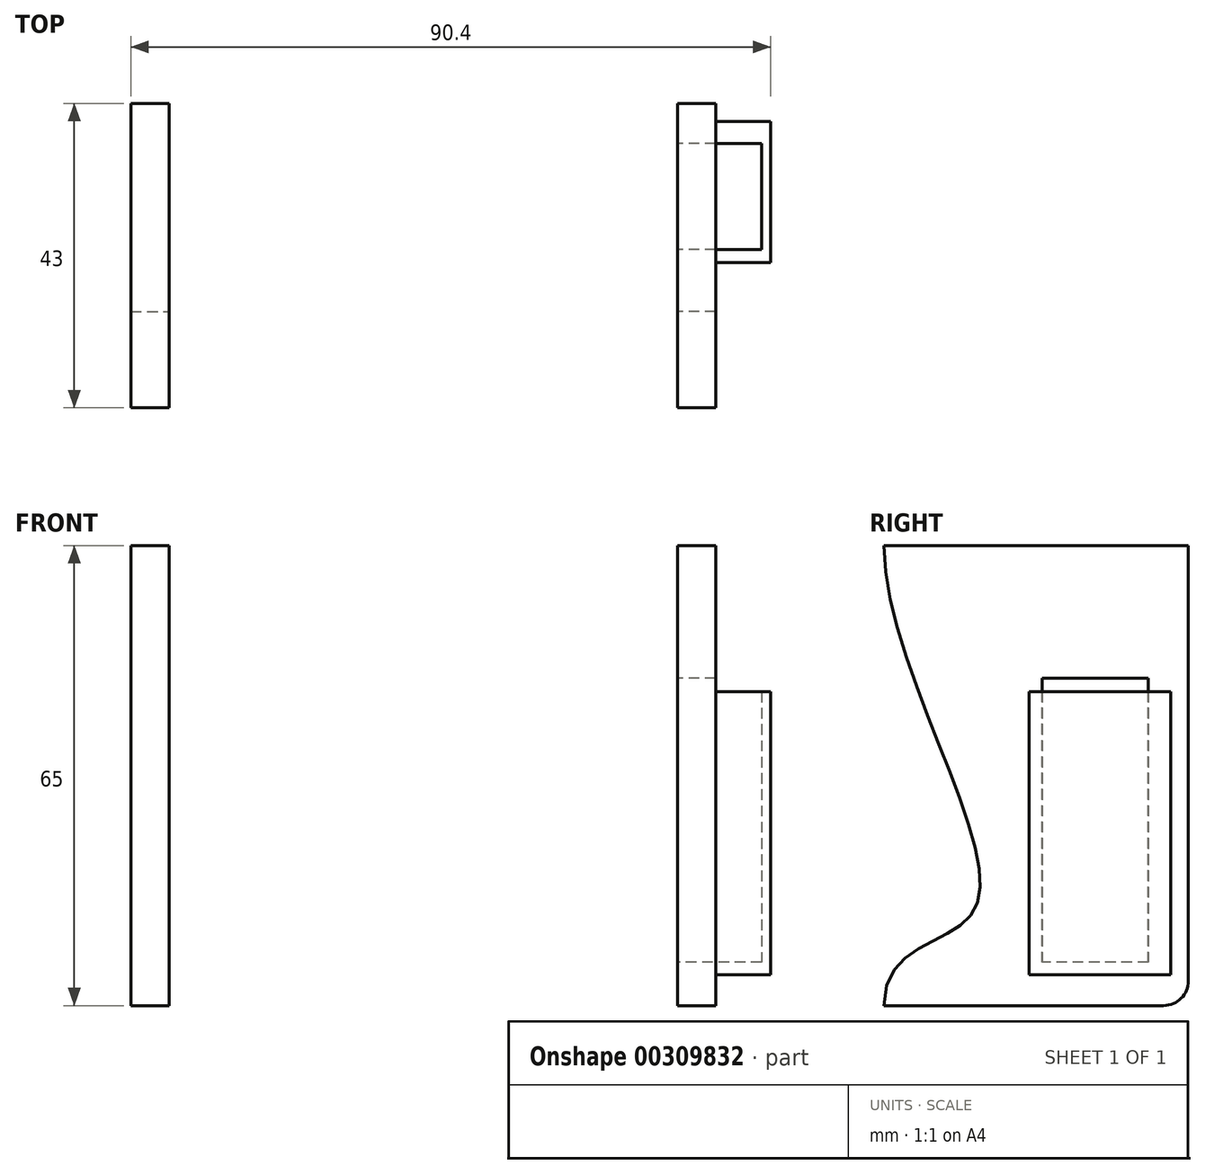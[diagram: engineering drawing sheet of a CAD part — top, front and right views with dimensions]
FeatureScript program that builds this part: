
annotation { "Feature Type Name" : "Feature", "Feature Type Description" : "" }
export const myFeature = defineFeature(function(context is Context, id is Id, definition is map)
    precondition{}
    {
        {
            var Q0;
            Q0=qCreatedBy(makeId("Top.planeOp"),FACE);
            var sketch = newSketch(context, id + "F0", { "sketchPlane" : qUnion([Q0])});
            skLineSegment(sketch, "E0.bottom", {"start": v(41.5, -22.5) * mm, "end": v(-41.5, -22.5) * mm});
            skLineSegment(sketch, "E0.top", {"start": v(41.5, 22.5) * mm, "end": v(-41.5, 22.5) * mm});
            skLineSegment(sketch, "E0.left", {"start": v(45, -19) * mm, "end": v(45, 19) * mm});
            skLineSegment(sketch, "E0.right", {"start": v(-45, -19) * mm, "end": v(-45, 19) * mm});
            skPoint(sketch, "E0.middle", {"position": v(0, 0) * mm});
            skCircle(sketch, "E1", {"center": v(-30, 7.5) * mm, "radius": 1.75 * mm});
            skLineSegment(sketch, "E2.top", {"start": v(-45, 7.5) * mm, "end": v(-30, 7.5) * mm, "construction": true});
            skLineSegment(sketch, "E2.right", {"start": v(-30, 22.5) * mm, "end": v(-30, 7.5) * mm, "construction": true});
            skCircle(sketch, "E3", {"center": v(-30, -7.5) * mm, "radius": 1.75 * mm});
            skLineSegment(sketch, "E4.bottom", {"start": v(-30, 22.5) * mm, "end": v(-15, 22.5) * mm, "construction": true});
            skLineSegment(sketch, "E4.top", {"start": v(-30, -22.5) * mm, "end": v(-15, -22.5) * mm, "construction": true});
            skLineSegment(sketch, "E4.left", {"start": v(-30, 22.5) * mm, "end": v(-30, -22.5) * mm, "construction": true});
            skLineSegment(sketch, "E4.right", {"start": v(-15, 22.5) * mm, "end": v(-15, -22.5) * mm, "construction": true});
            skLineSegment(sketch, "E5.bottom", {"start": v(-15, 22.5) * mm, "end": v(0, 22.5) * mm, "construction": true});
            skLineSegment(sketch, "E5.top", {"start": v(-15, -22.5) * mm, "end": v(0, -22.5) * mm, "construction": true});
            skLineSegment(sketch, "E5.right", {"start": v(0, 22.5) * mm, "end": v(0, -22.5) * mm, "construction": true});
            skLineSegment(sketch, "E6.bottom", {"start": v(0, 22.5) * mm, "end": v(15, 22.5) * mm, "construction": true});
            skLineSegment(sketch, "E6.top", {"start": v(0, -22.5) * mm, "end": v(15, -22.5) * mm, "construction": true});
            skLineSegment(sketch, "E6.right", {"start": v(15, 22.5) * mm, "end": v(15, -22.5) * mm, "construction": true});
            skLineSegment(sketch, "E7.bottom", {"start": v(15, 22.5) * mm, "end": v(30, 22.5) * mm, "construction": true});
            skLineSegment(sketch, "E7.top", {"start": v(15, -22.5) * mm, "end": v(30, -22.5) * mm, "construction": true});
            skLineSegment(sketch, "E7.right", {"start": v(30, 22.5) * mm, "end": v(30, -22.5) * mm, "construction": true});
            skLineSegment(sketch, "E8", {"start": v(-45, 7.5) * mm, "end": v(45, 7.5) * mm, "construction": true});
            skCircle(sketch, "E9", {"center": v(-15, 7.5) * mm, "radius": 1.75 * mm});
            skCircle(sketch, "E10", {"center": v(-15, -7.5) * mm, "radius": 1.75 * mm});
            skCircle(sketch, "E11", {"center": v(0, 7.5) * mm, "radius": 1.75 * mm});
            skCircle(sketch, "E12", {"center": v(0, -7.5) * mm, "radius": 1.75 * mm});
            skCircle(sketch, "E13", {"center": v(15.11, 7.5) * mm, "radius": 1.75 * mm});
            skCircle(sketch, "E14", {"center": v(15, -7.5) * mm, "radius": 1.75 * mm});
            skCircle(sketch, "E15", {"center": v(30, 7.5) * mm, "radius": 1.75 * mm});
            skCircle(sketch, "E16", {"center": v(30, -7.5) * mm, "radius": 1.75 * mm});
            skPoint(sketch, "E17.visualSharp", {"position": v(-45, 22.5) * mm});
            skArc(sketch, "E17.filletArc", {"start": v(-41.5, 22.5) * mm, "mid": v(-43.97, 21.47) * mm, "end": v(-45, 19) * mm});
            skPoint(sketch, "E18.visualSharp", {"position": v(-45, -22.5) * mm});
            skArc(sketch, "E18.filletArc", {"start": v(-45, -19) * mm, "mid": v(-43.97, -21.47) * mm, "end": v(-41.5, -22.5) * mm});
            skPoint(sketch, "E19.visualSharp", {"position": v(45, 22.5) * mm});
            skArc(sketch, "E19.filletArc", {"start": v(45, 19) * mm, "mid": v(43.97, 21.47) * mm, "end": v(41.5, 22.5) * mm});
            skPoint(sketch, "E20.visualSharp", {"position": v(45, -22.5) * mm});
            skArc(sketch, "E20.filletArc", {"start": v(41.5, -22.5) * mm, "mid": v(43.97, -21.47) * mm, "end": v(45, -19) * mm});
            skSolve(sketch);
        }
        {
            var Q0;
            Q0 = qSketchRegion(id + "F0", true);
            extrude(context, id + "F1", {"entities" : qUnion([Q0]), "depth" : 3 * mm});
        }
        {
            var Q0;
            Q0=qCreatedBy(makeId("Right.planeOp"),FACE);
            var sketch = newSketch(context, id + "F2", { "sketchPlane" : qUnion([Q0])});
            skLineSegment(sketch, "E21.bottom", {"start": v(20.67, 0) * mm, "end": v(-22.33, 0) * mm});
            skLineSegment(sketch, "E21.top", {"start": v(17.17, -65) * mm, "end": v(-22.33, -65) * mm});
            skLineSegment(sketch, "E21.left", {"start": v(20.67, 0) * mm, "end": v(20.67, -61.5) * mm});
            skFitSpline(sketch, "E22", {"points": [v(-22.33, 0) * mm, v(-9.46, -51.3) * mm, v(-22.33, -65) * mm], "startDerivative": vector(0, -82.73) * mm, "endDerivative": vector(0, -74.1) * mm});
            skPoint(sketch, "E23.visualSharp", {"position": v(20.67, -65) * mm});
            skArc(sketch, "E23.filletArc", {"start": v(17.17, -65) * mm, "mid": v(19.64, -63.97) * mm, "end": v(20.67, -61.5) * mm});
            skLineSegment(sketch, "E24.filletArc", {"start": v(-22.33, 0) * mm, "end": v(-22.33, 0) * mm});
            skSolve(sketch);
        }
        {
            var Q0;
            Q0=makeQuery(id+"F2.imprint","IMPRINT",FACE,{"disambiguationData":[TD([[makeQuery(id+"F2.imprint","IMPRINT",EDGE,{"derivedFrom":sQuery(id+"F2.wireOp",EDGE,"E21.bottom")}),1.0]])]});
            var Q1;
            Q1 = qSketchRegion(id + "F4", true);
            extrude(context, id + "F3", {"entities" : qUnion([Q0, Q1]), "operationType" : NewBodyOperationType.ADD, "endBound" : BoundingType.SYMMETRIC, "depth" : 82.6 * mm});
        }
        {
            var Q0;
            Q0=qCreatedBy(makeId("Right.planeOp"),FACE);
            var sketch = newSketch(context, id + "F4", { "sketchPlane" : qUnion([Q0])});
            skLineSegment(sketch, "E25.bottom", {"start": v(20.9, 0) * mm, "end": v(-22.1, 0) * mm});
            skLineSegment(sketch, "E25.top", {"start": v(17.4, -65) * mm, "end": v(-22.1, -65) * mm});
            skLineSegment(sketch, "E25.left", {"start": v(20.9, 0) * mm, "end": v(20.9, -61.5) * mm});
            skFitSpline(sketch, "E26", {"points": [v(-22.1, 0) * mm, v(-9.21, -51.28) * mm, v(-22.1, -65) * mm], "startDerivative": vector(0, -82.73) * mm, "endDerivative": vector(0, -74.1) * mm});
            skPoint(sketch, "E27.visualSharp", {"position": v(20.9, -65) * mm});
            skArc(sketch, "E27.filletArc", {"start": v(17.4, -65) * mm, "mid": v(19.88, -63.97) * mm, "end": v(20.9, -61.5) * mm});
            skLineSegment(sketch, "E28.filletArc", {"start": v(-22.1, 0) * mm, "end": v(-22.1, 0) * mm});
            skSolve(sketch);
        }
        {
            var Q0;
            Q0=makeQuery(id+"F3.opExtrude","CAP_FACE",FACE,{"disambiguationData":[OSD([sQuery(id+"F2.wireOp",EDGE,"E21.bottom"),sQuery(id+"F2.wireOp",EDGE,"E21.top"),sQuery(id+"F2.wireOp",EDGE,"E21.left"),sQuery(id+"F2.wireOp",EDGE,"E22"),sQuery(id+"F2.wireOp",EDGE,"E23.filletArc")])],"isStart":true});
            var Q1;
            Q1=makeQuery(id+"F3.opExtrude","CAP_FACE",FACE,{"disambiguationData":[OSD([sQuery(id+"F2.wireOp",EDGE,"E21.bottom"),sQuery(id+"F2.wireOp",EDGE,"E21.top"),sQuery(id+"F2.wireOp",EDGE,"E21.left"),sQuery(id+"F2.wireOp",EDGE,"E22"),sQuery(id+"F2.wireOp",EDGE,"E23.filletArc")])],"isStart":false});
            extrude(context, id + "F5", {"entities" : qUnion([Q0, Q1]), "operationType" : NewBodyOperationType.INTERSECT, "endBound" : BoundingType.SYMMETRIC, "oppositeDirection" : true, "depth" : 10.8 * mm});
        }
        {
            var Q0;
            Q0=qCreatedBy(makeId("Right.planeOp"),FACE);
            var sketch = newSketch(context, id + "F6", { "sketchPlane" : qUnion([Q0])});
            skLineSegment(sketch, "E29.bottom", {"start": v(18.14, -20.64) * mm, "end": v(-1.86, -20.64) * mm});
            skLineSegment(sketch, "E29.top", {"start": v(18.14, -60.64) * mm, "end": v(-1.86, -60.64) * mm});
            skLineSegment(sketch, "E29.left", {"start": v(18.14, -20.64) * mm, "end": v(18.14, -60.64) * mm});
            skLineSegment(sketch, "E29.right", {"start": v(-1.86, -20.64) * mm, "end": v(-1.86, -60.64) * mm});
            skSolve(sketch);
        }
        {
            var Q0;
            Q0 = qSketchRegion(id + "F6", true);
            extrude(context, id + "F7", {"entities" : qUnion([Q0]), "operationType" : NewBodyOperationType.ADD, "depth" : 49.1 * mm});
        }
        {
            var Q0;
            {var subQ5=sQuery(id+"F6.wireOp",EDGE,"E29.top");var subQ6=sQuery(id+"F6.wireOp",EDGE,"E29.bottom");var subQ7=sQuery(id+"F6.wireOp",EDGE,"E29.left");Q0=makeQuery(id+"F7.boolean.opBoolean","SPLIT",FACE,{"disambiguationData":[TD([makeQuery(id+"F7.opExtrude","CAP_FACE",FACE,{"disambiguationData":[OSD([subQ6,subQ5,subQ7,sQuery(id+"F6.wireOp",EDGE,"E29.right")])],"isStart":true})])],"derivedFrom":makeQuery(id+"F7.opExtrude","SWEPT_FACE",FACE,{"disambiguationData":[OSD([subQ7])]})});}
            var Q1;
            Q1 = qConstructionFilter(qBodyType(qCreatedBy(id + "F6" ,EDGE), BodyType.WIRE), ConstructionObject.NO);
            extrude(context, id + "F8", {"entities" : qUnion([Q0]), "operationType" : NewBodyOperationType.REMOVE, "surfaceEntities" : qUnion([Q1]), "oppositeDirection" : true, "depth" : 25 * mm});
        }
        {
            var Q0;
            Q0=qCreatedBy(makeId("Right.planeOp"),FACE);
            var sketch = newSketch(context, id + "F9", { "sketchPlane" : qUnion([Q0])});
            skLineSegment(sketch, "E30.bottom", {"start": v(0, -18.72) * mm, "end": v(15, -18.72) * mm});
            skLineSegment(sketch, "E30.top", {"start": v(0, -58.87) * mm, "end": v(15, -58.87) * mm});
            skLineSegment(sketch, "E30.left", {"start": v(0, -18.72) * mm, "end": v(0, -58.87) * mm});
            skLineSegment(sketch, "E30.right", {"start": v(15, -18.72) * mm, "end": v(15, -58.87) * mm});
            skSolve(sketch);
        }
        {
            var Q0;
            Q0 = qSketchRegion(id + "F9", true);
            extrude(context, id + "F10", {"entities" : qUnion([Q0]), "operationType" : NewBodyOperationType.REMOVE, "depth" : 47.8 * mm});
        }
    });
